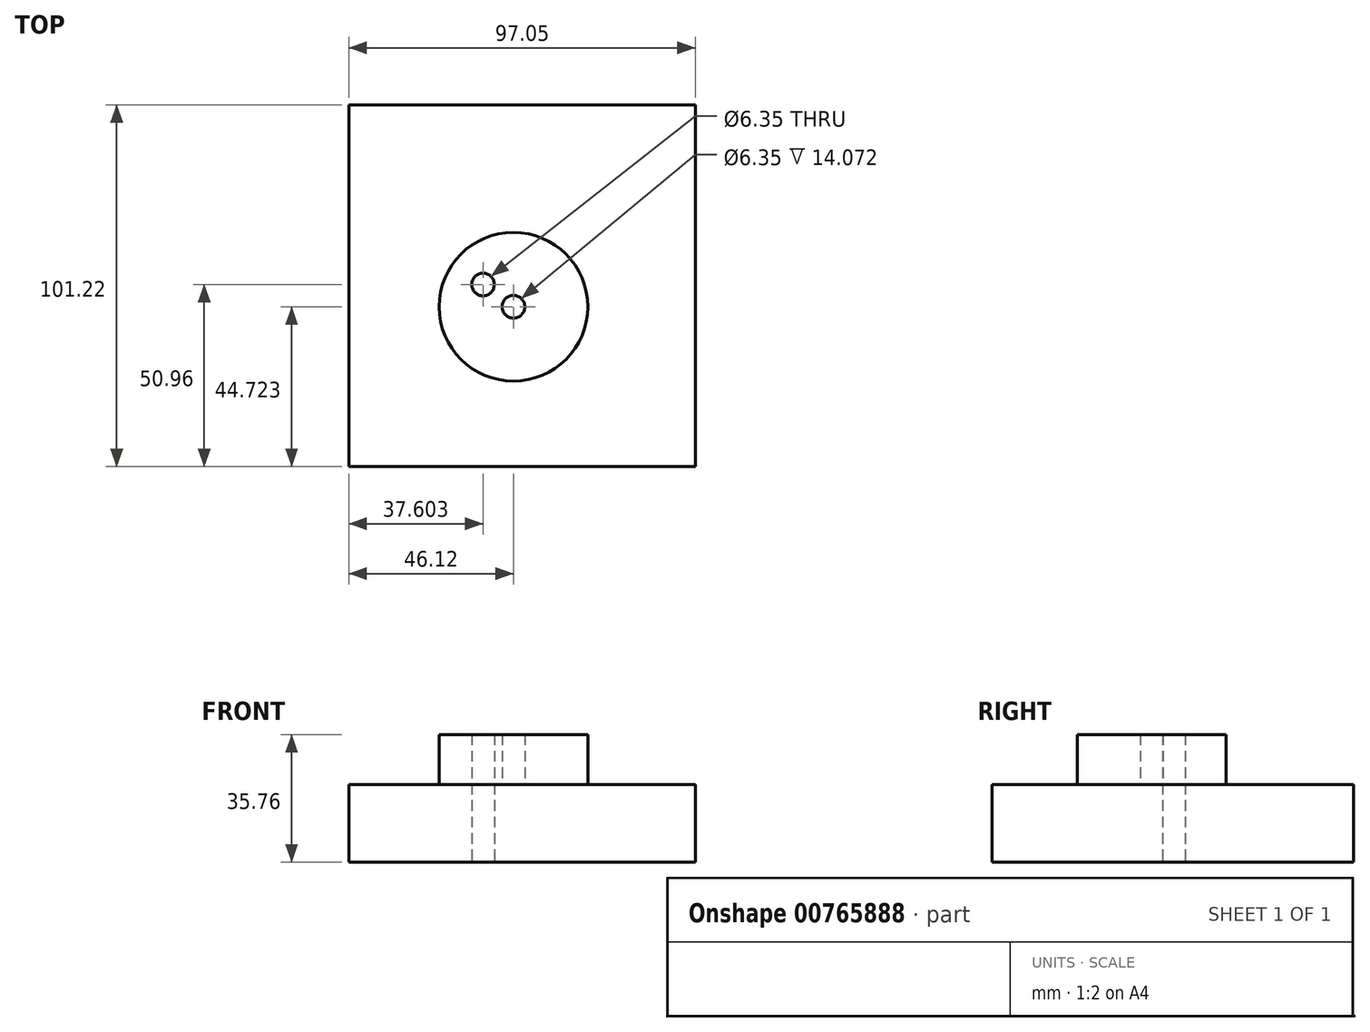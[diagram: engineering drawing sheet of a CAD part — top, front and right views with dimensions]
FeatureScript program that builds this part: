
annotation { "Feature Type Name" : "Feature", "Feature Type Description" : "" }
export const myFeature = defineFeature(function(context is Context, id is Id, definition is map)
    precondition{}
    {
        {
            var Q0;
            Q0=qCreatedBy(makeId("Top.planeOp"),FACE);
            var sketch = newSketch(context, id + "F0", { "sketchPlane" : qUnion([Q0])});
            skLineSegment(sketch, "E0", {"start": v(-46.12, 50.26) * mm, "end": v(-46.12, -50.96) * mm});
            skLineSegment(sketch, "E1", {"start": v(-46.12, -50.96) * mm, "end": v(50.93, -50.96) * mm});
            skLineSegment(sketch, "E2", {"start": v(50.93, -50.96) * mm, "end": v(50.93, 48.69) * mm});
            skLineSegment(sketch, "E3", {"start": v(50.93, 48.69) * mm, "end": v(50.93, 50.26) * mm});
            skLineSegment(sketch, "E4", {"start": v(50.93, 50.26) * mm, "end": v(-46.12, 50.26) * mm});
            skSolve(sketch);
        }
        {
            var Q0;
            Q0=makeQuery(id+"F0.imprint","IMPRINT",FACE,{"disambiguationData":[TD([[makeQuery(id+"F0.imprint","IMPRINT",EDGE,{"derivedFrom":sQuery(id+"F0.wireOp",EDGE,"E0")}),1.0]])]});
            extrude(context, id + "F1", {"entities" : qUnion([Q0]), "depth" : 21.68 * mm, "offsetDistance" : 25.4 * mm});
        }
        {
            var Q0;
            Q0=makeQuery(id+"F1.opExtrude","CAP_FACE",FACE,{"disambiguationData":[OSD([sQuery(id+"F0.wireOp",EDGE,"E0"),sQuery(id+"F0.wireOp",EDGE,"E1"),sQuery(id+"F0.wireOp",EDGE,"E2"),sQuery(id+"F0.wireOp",EDGE,"E3"),sQuery(id+"F0.wireOp",EDGE,"E4")])],"isStart":false});
            var sketch = newSketch(context, id + "F2", { "sketchPlane" : qUnion([Q0])});
            skCircle(sketch, "E5", {"center": v(0, -6.24) * mm, "radius": 20.82 * mm});
            skSolve(sketch);
        }
        {
            var Q0;
            Q0 = qSketchRegion(id + "F2", true);
            var Q1;
            Q1=makeQuery(id+"F2.imprint","IMPRINT",FACE,{"disambiguationData":[TD([[makeQuery(id+"F2.imprint","IMPRINT",EDGE,{"derivedFrom":sQuery(id+"F2.wireOp",EDGE,"E5")}),1.0]])]});
            extrude(context, id + "F3", {"entities" : qUnion([Q0, Q1]), "operationType" : NewBodyOperationType.ADD, "depth" : 14.07 * mm, "offsetDistance" : 25.4 * mm});
        }
        {
            var Q0;
            Q0=qCreatedBy(makeId("Front.planeOp"),FACE);
            var sketch = newSketch(context, id + "F4", { "sketchPlane" : qUnion([Q0])});
            skLineSegment(sketch, "E6", {"start": v(-12.02, 22.06) * mm, "end": v(0, 35) * mm});
            skLineSegment(sketch, "E7", {"start": v(0, 35) * mm, "end": v(0, 21.61) * mm});
            skLineSegment(sketch, "E8", {"start": v(0, 21.61) * mm, "end": v(-12.02, 22.06) * mm});
            skSolve(sketch);
        }
        {
            var Q0;
            Q0=sQuery(id+"F4.wireOp",EDGE,"E6");
            var Q1;
            Q1=sQuery(id+"F4.wireOp",EDGE,"E7");
            var Q2;
            Q2=sQuery(id+"F4.wireOp",EDGE,"E8");
            extrude(context, id + "F5", {"bodyType" : ToolBodyType.SURFACE, "surfaceEntities" : qUnion([Q0, Q1, Q2]), "depth" : 25.4 * mm, "offsetDistance" : 25.4 * mm});
        }
        {
            var Q0;
            Q0=qCreatedBy(makeId("Top.planeOp"),FACE);
            var sketch = newSketch(context, id + "F6", { "sketchPlane" : qUnion([Q0])});
            skCircle(sketch, "E9", {"center": v(-8.52, 0) * mm, "radius": 15.8 * mm});
            skSolve(sketch);
        }
        {
            var Q0;
            Q0=sQuery(id+"F2.wireOp",VERTEX,"E5.center");
            var Q1;
            Q1=sQuery(id+"F6.wireOp",VERTEX,"E9.center");
            var Q2;
            Q2=makeQuery(id+"F1.opExtrude","SWEPT_BODY",BODY,{"disambiguationData":[OSD([sQuery(id+"F0.wireOp",EDGE,"E0"),sQuery(id+"F0.wireOp",EDGE,"E1"),sQuery(id+"F0.wireOp",EDGE,"E2"),sQuery(id+"F0.wireOp",EDGE,"E3"),sQuery(id+"F0.wireOp",EDGE,"E4")])]});
            hole(context, id + "F7", {"style" : HoleStyle.SIMPLE, "endStyle" : HoleEndStyle.THROUGH, "oppositeDirection" : true, "holeDiameter" : 6.35 * mm, "majorDiameter" : 6.35 * mm, "isTappedThrough" : true, "tappedDepth" : 12.7 * mm, "tapClearance" : 3, "locations" : qUnion([Q0, Q1]), "scope" : qUnion([Q2])});
        }
    });
